# Revit family: RLS1-LED-xxWS-xxxTx
name_source: partatom
category: Leuchten
revit_build: Autodesk Revit 2017 (Build: 20190508_0315(x64)
units: mm (PartAtom-declared; Revit-internal decimal feet)

## family parameters
Basisbauteil = Fläche
Beim Laden mit Abzugskörper schneiden = Nein
Bemaßung runder Anschluss = Durchmesser verwenden
Gemeinsam genutzt = Nein
Lichtquelle = Ja
OmniClass-Nummer = 23.80.70.11
OmniClass-Titel = Luminaries for Internal Lighting
Raumberechnungspunkt = Nein
Teiletyp = Normal

## types (12) — shared parameters
Baugruppenkennzeichen = D5020200
Emissionsform beim Rendern sichtbar = Nein
Farbfilter = 16777215
Farbtemperaturverschiebung bei Dämpfen der Lampe = <Keine Auswahl>
Hersteller = RIDI Leuchten GmbH
Lampe = LED
Neigungswinkel = 90.00°
URL = www.ridi.de
Von Kreisdurchmesser aussenden = 224 mm  [stored 0.734908 ft]
brand = RIDI
conformity mark = CE
electrical safety class = 1
height = 380 mm
ingress protection (IP) code = IP65
length = 270 mm  [stored 0.885827 ft]
nominal frequency = 50-60Hz
nominal voltage = 230
voltage type (AC, DC, UC) = AC
width = 270 mm  [stored 0.885827 ft]
zero-valued in all types: Vorgabe-Ansicht

## per-type parameters (varying)
| type | Datei für fotometrisches Netz | Modell | Scheinlast | rated input power | weight |
| RLS1-LED NDWS-500T830 | RLS1-LED NDWS-500T840.IES | 0321475 | 47 VA | 47 | 4,22 kg |
| RLS1-LED DAWS-500T830 | RLS1-LED NDWS-500T840.IES | 0331475 | 47 VA | 47 | 4,24 kg |
| RLS1-LED NDWS-500T840 | RLS1-LED NDWS-500T840.IES | 0321476 | 47 VA | 47 | 4,22 kg |
| RLS1-LED DAWS-500T840 | RLS1-LED NDWS-500T840.IES | 0331476 | 47 VA | 47 | 4,24 kg |
| RLS1-LED NDWS-1000T830 | RLS1-LED NDWS-1000T840.IES | 0321477 | 80 VA | 80 | 4,28 kg |
| RLS1-LED DAWS-1000T830 | RLS1-LED NDWS-1000T840.IES | 0331477 | 80 VA | 80 | 5 kg |
| RLS1-LED NDWS-1000T840 | RLS1-LED NDWS-1000T840.IES | 0321478 | 80 VA | 80 | 4,28 kg |
| RLS1-LED DAWS-1000T840 | RLS1-LED NDWS-1000T840.IES | 0331478 | 80 VA | 80 | 5 kg |
| RLS1-LED NDWS-1600T830 | RLS1-LED NDWS-1600T840.IES | 0321479 | 115 VA | 115 | 5 kg |
| RLS1-LED DAWS-1600T830 | RLS1-LED NDWS-1600T840.IES | 0331479 | 115 VA | 115 | 5,8 kg |
| RLS1-LED NDWS-1600T840 | RLS1-LED NDWS-1600T840.IES | 0321480 | 115 VA | 115 | 5 kg |
| RLS1-LED DAWS-1600T840 | RLS1-LED NDWS-1600T840.IES | 0331480 | 115 VA | 115 | 5,8 kg |

note: column(s) folded — value = type name in every type: product name

note: [stored X ft] marks values corroborated as IEEE doubles in the binary element streams (Revit-internal decimal feet)
